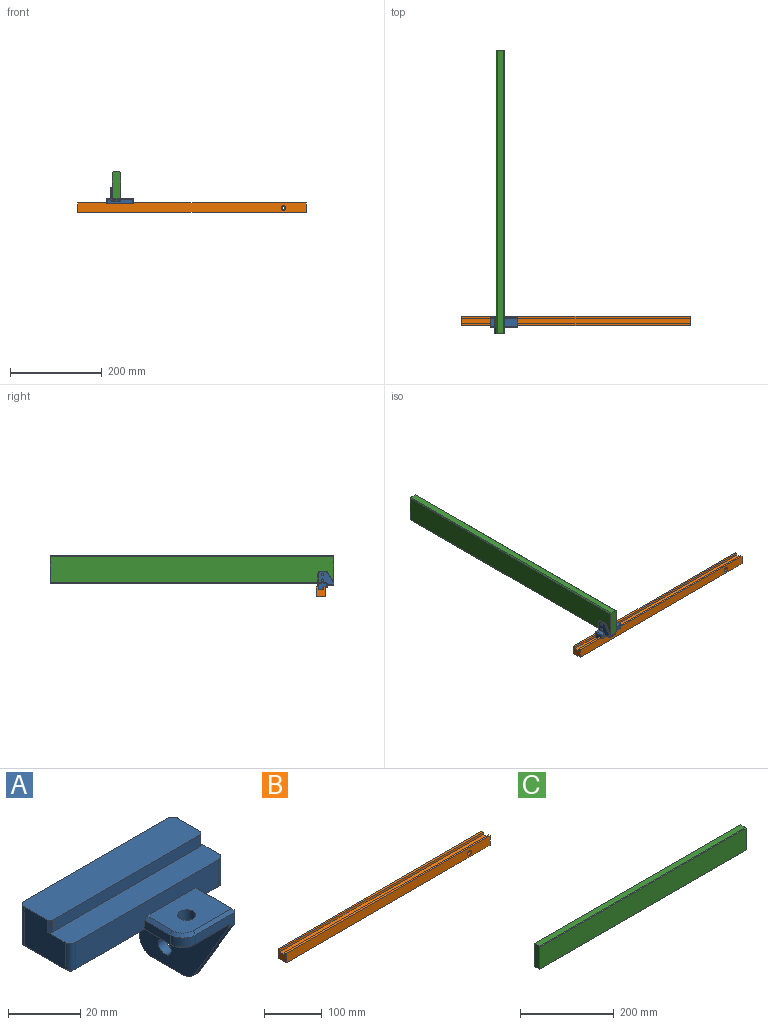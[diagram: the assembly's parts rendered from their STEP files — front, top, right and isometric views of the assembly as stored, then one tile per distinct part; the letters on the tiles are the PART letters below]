
ASSEMBLY  parts=3 mates=2
PART A: 51 faces, bbox 60x35x39 mm
  f0: plane 46x33mm, normal (0,0,-1), area 1059.5mm2, adj f15,f17,f35,f36,f37,f38,f39,f40
  f1: plane 56x9mm, normal (0,-1,0), area 421mm2, adj f2,f8,f10,f11,f12,f13,f25,f39
  f2: cylinder r=2mm len=9mm, axis (0,0,1), area 28.3mm2, adj f1,f3,f10,f27
  f3: plane 16x13mm, normal (1,0,0), area 180mm2, adj f2,f4,f10,f29,f44,f49
  f4: cylinder r=2mm len=13mm, axis (0,0,1), area 40.8mm2, adj f3,f5,f31,f44
  f5: plane 56x34mm, normal (0,1,0), area 770mm2, adj f4,f6,f15,f23,f33,f34,f35,f44
  f6: cylinder r=2mm len=13mm, axis (0,0,1), area 40.8mm2, adj f5,f7,f36,f44
  f7: plane 16x13mm, normal (-1,0,0), area 180mm2, adj f6,f8,f10,f37,f44,f50
  f8: cylinder r=2mm len=9mm, axis (0,0,1), area 28.3mm2, adj f1,f7,f10,f38
  f9: plane 18x9mm, normal (0,0,-1), area 161.6mm2, adj f12,f25,f27,f29,f31,f33
  f10: plane 60x9mm, normal (0,0,1), area 479.3mm2, adj f1,f2,f3,f7,f8,f43,f49,f50
  f11: plane 10x3mm, normal (-1,0,0), area 30mm2, adj f1,f18,f40,f48
  f12: plane 33x28mm, normal (1,0,0), area 628.2mm2, adj f1,f9,f20,f21,f24,f25,f26,f28
  f13: plane 19x14mm, normal (0,0,1), area 242.9mm2, adj f1,f17,f45,f46,f47,f48
  f14: plane 15x4mm, normal (0,-1,0), area 47mm2, adj f15,f18,f19,f24,f42,f46
  f15: plane 35x26mm, normal (-1,0,0), area 642.6mm2, adj f0,f5,f14,f16,f19,f20,f21,f22
  f16: plane 12.17x2mm, normal (0,0,-1), area 24.3mm2, adj f15,f22,f23,f30
  f17: cylinder r=2.5mm len=5mm, axis (0,0,-1), area 78.5mm2, adj f0,f13
  f18: cylinder r=5mm len=5mm, axis (0,0,1), area 23.6mm2, adj f11,f14,f41,f47
  f19: plane 22.57x13.54mm, normal (0,-0.86,-0.51), area 52.6mm2, adj f14,f15,f22,f26
  f20: cylinder r=2.5mm len=5mm, axis (1,0,0), area 47.1mm2, adj f12,f15
  f21: cylinder r=2.5mm len=5mm, axis (1,0,0), area 47.1mm2, adj f12,f15
  f22: cylinder r=5mm len=4.29mm, axis (1,0,0), area 10.3mm2, adj f15,f16,f19,f28
  f23: cylinder r=5mm len=5mm, axis (-1,0,0), area 15.7mm2, adj f5,f15,f16,f32
  f24: plane 4.5x1mm, normal (0.71,-0.71,0), area 5.8mm2, adj f12,f14,f26,f45,f46
  f25: plane 8x1mm, normal (0,-0.71,-0.71), area 11.3mm2, adj f1,f9,f12,f27
  f26: plane 22.85x14.4mm, normal (0.71,-0.61,-0.36), area 37mm2, adj f12,f19,f24,f28
  f27: cone r=2mm half-angle=45deg, axis (0,0,1), area 3.3mm2, adj f2,f9,f25,f29
  f28: cone r=4mm half-angle=45deg, axis (-1,0,0), area 6.6mm2, adj f12,f22,f26,f30
  f29: plane 16x1mm, normal (0.71,0,-0.71), area 22.6mm2, adj f3,f9,f27,f31
  f30: plane 12.17x1mm, normal (0.71,0,-0.71), area 17.2mm2, adj f12,f16,f28,f32
  f31: cone r=2mm half-angle=45deg, axis (0,0,1), area 3.3mm2, adj f4,f9,f29,f33
  f32: cone r=4mm half-angle=45deg, axis (-1,0,0), area 10mm2, adj f12,f23,f30,f34
  f33: plane 9x1mm, normal (0,0.71,-0.71), area 12mm2, adj f5,f9,f31,f34
  f34: plane 21x1mm, normal (0.71,0.71,0), area 29mm2, adj f5,f12,f32,f33
  f35: plane 45x1mm, normal (0,0.71,-0.71), area 63.6mm2, adj f0,f5,f15,f36
  f36: cone r=2mm half-angle=45deg, axis (0,0,1), area 3.3mm2, adj f0,f6,f35,f37
  f37: plane 16x1mm, normal (-0.71,0,-0.71), area 22.6mm2, adj f0,f7,f36,f38
  f38: cone r=2mm half-angle=45deg, axis (0,0,1), area 3.3mm2, adj f0,f8,f37,f39
  f39: plane 28x1mm, normal (0,-0.71,-0.71), area 38.9mm2, adj f0,f1,f38,f40
  f40: plane 11x1mm, normal (-0.71,0,-0.71), area 14.8mm2, adj f0,f11,f39,f41
  f41: cone r=4mm half-angle=45deg, axis (0,0,1), area 10mm2, adj f0,f18,f40,f42
  f42: plane 13x1mm, normal (0,-0.71,-0.71), area 18.4mm2, adj f0,f14,f15,f41
  f43: plane 58x4mm, normal (0,-1,0), area 232mm2, adj f10,f44,f49,f50
  f44: plane 60x12mm, normal (0,0,1), area 717.3mm2, adj f3,f4,f5,f6,f7,f43,f49,f50
  f45: plane 14.5x1mm, normal (0.71,0,0.71), area 20.2mm2, adj f1,f12,f13,f24,f46
  f46: plane 15.5x1mm, normal (0,-0.71,0.71), area 21.6mm2, adj f13,f14,f24,f45,f47
  f47: cone r=4mm half-angle=45deg, axis (0,0,-1), area 10mm2, adj f13,f18,f46,f48
  f48: plane 10x1mm, normal (-0.71,0,0.71), area 14.1mm2, adj f1,f11,f13,f47
  f49: plane 4x1mm, normal (0.71,-0.71,0), area 5.7mm2, adj f3,f10,f43,f44
  f50: plane 4x1mm, normal (-0.71,-0.71,0), area 5.7mm2, adj f7,f10,f43,f44
PART B: 13 faces, bbox 500x20x20 mm
  f0: cylinder r=3mm len=14mm, axis (0,-1,0), area 263.9mm2, adj f5,f12
  f1: plane 500x4mm, normal (0,0,1), area 2000mm2, adj f2,f3,f4,f8
  f2: plane 20x20mm, normal (-1,0,0), area 340mm2, adj f1,f3,f5,f6,f7,f8,f9,f10
  f3: plane 500x20mm, normal (0,-1,0), area 9921.5mm2, adj f1,f2,f4,f7,f11
  f4: plane 20x20mm, normal (1,0,0), area 340mm2, adj f1,f3,f5,f6,f7,f8,f9,f10
  f5: plane 500x20mm, normal (0,1,0), area 9971.7mm2, adj f0,f2,f4,f6,f7
  f6: plane 500x4mm, normal (0,0,1), area 2000mm2, adj f2,f4,f5,f9
  f7: plane 500x20mm, normal (0,0,-1), area 10000mm2, adj f2,f3,f4,f5
  f8: plane 500x5mm, normal (0,1,0), area 2500mm2, adj f1,f2,f4,f10
  f9: plane 500x5mm, normal (0,-1,0), area 2500mm2, adj f2,f4,f6,f10
  f10: plane 500x12mm, normal (0,0,1), area 6000mm2, adj f2,f4,f8,f9
  f11: cylinder r=5mm len=10mm, axis (0,-1,0), area 188.5mm2, adj f3,f12
  f12: plane 10x10mm, normal (0,-1,0), area 50.3mm2, adj f0,f11
PART C: 10 faces, bbox 620x18x60 mm
  f0: plane 620x56mm, normal (0,-1,0), area 34720mm2, adj f1,f3,f8,f9
  f1: plane 60x18mm, normal (1,0,0), area 1072mm2, adj f0,f2,f4,f5,f6,f7,f8,f9
  f2: plane 620x56mm, normal (0,1,0), area 34720mm2, adj f1,f3,f6,f7
  f3: plane 60x18mm, normal (-1,0,0), area 1072mm2, adj f0,f2,f4,f5,f6,f7,f8,f9
  f4: plane 620x14mm, normal (0,0,1), area 8680mm2, adj f1,f3,f7,f8
  f5: plane 620x14mm, normal (0,0,-1), area 8680mm2, adj f1,f3,f6,f9
  f6: plane 620x2mm, normal (0,0.71,-0.71), area 1753.6mm2, adj f1,f2,f3,f5
  f7: plane 620x2mm, normal (0,0.71,0.71), area 1753.6mm2, adj f1,f2,f3,f4
  f8: plane 620x2mm, normal (0,-0.71,0.71), area 1753.6mm2, adj f0,f1,f3,f4
  f9: plane 620x2mm, normal (0,-0.71,-0.71), area 1753.6mm2, adj f0,f1,f3,f5
PLACE A rot(axis=(0,1,0),180deg) t=(-177.28,-21.84,21.45)mm
PLACE B t=(-20.28,-18.34,2.45)mm
PLACE C rot(axis=(0,0,-1),90deg) t=(-185.28,263.16,30.45)mm
MATE fastened C.f1 <-> A.f14  axis (0,-1,0) through (-185.28,-46.84,30.45)mm
MATE slider A.f3 <-> B.f2  axis (-1,0,0) through (-207.28,-18.34,17.45)mm
